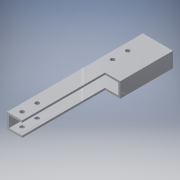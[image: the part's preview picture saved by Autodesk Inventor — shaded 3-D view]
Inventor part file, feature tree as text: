
AUTODESK INVENTOR PART (.ipt)
format: ipt  version: 2016 (Build 200138000, 138)  size: 138,240 bytes
history: native  units: in
note: dims shown in document units (in); Inventor stores cm internally (conversion verified against a paired STEP export)
features: extrude x4, sketch x4
ambient origin geometry x8: Origin, YZ Plane, XZ Plane, XY Plane, X Axis, Y Axis, Z Axis, Center Point
bodies: Solid1 (feature_tree)
feature tree (8):
  extrude  "Extrusion1"  Depth=1.0in
  extrude  "Extrusion2"  Depth=9.0in TaperAngle=0.0deg
  extrude  "Extrusion3"  Depth=5.5in
  extrude  "Extrusion4"  Depth=1.0in
  sketch  "Sketch1"  dims[d0=2.0in d1=1.0in]
  sketch  "Sketch2"  dims[d2=0.125in d3=9.0in d4=0.0in]
  sketch  "Sketch3"  dims[d5=1.0in d6=5.5in]
  sketch  "Sketch4"  dims[d7=1.0in d8=0.0in d9=0.2656in d10=0.2656in d11=0.5in d12=0.5in d13=0.5in d14=1.5in d15=1.0in d16=0.0in d17=0.2656in d18=0.266in d19=2.0in d20=0.5in d21=0.5in d22=1.0in d23=1.0in d24=0.0in]
